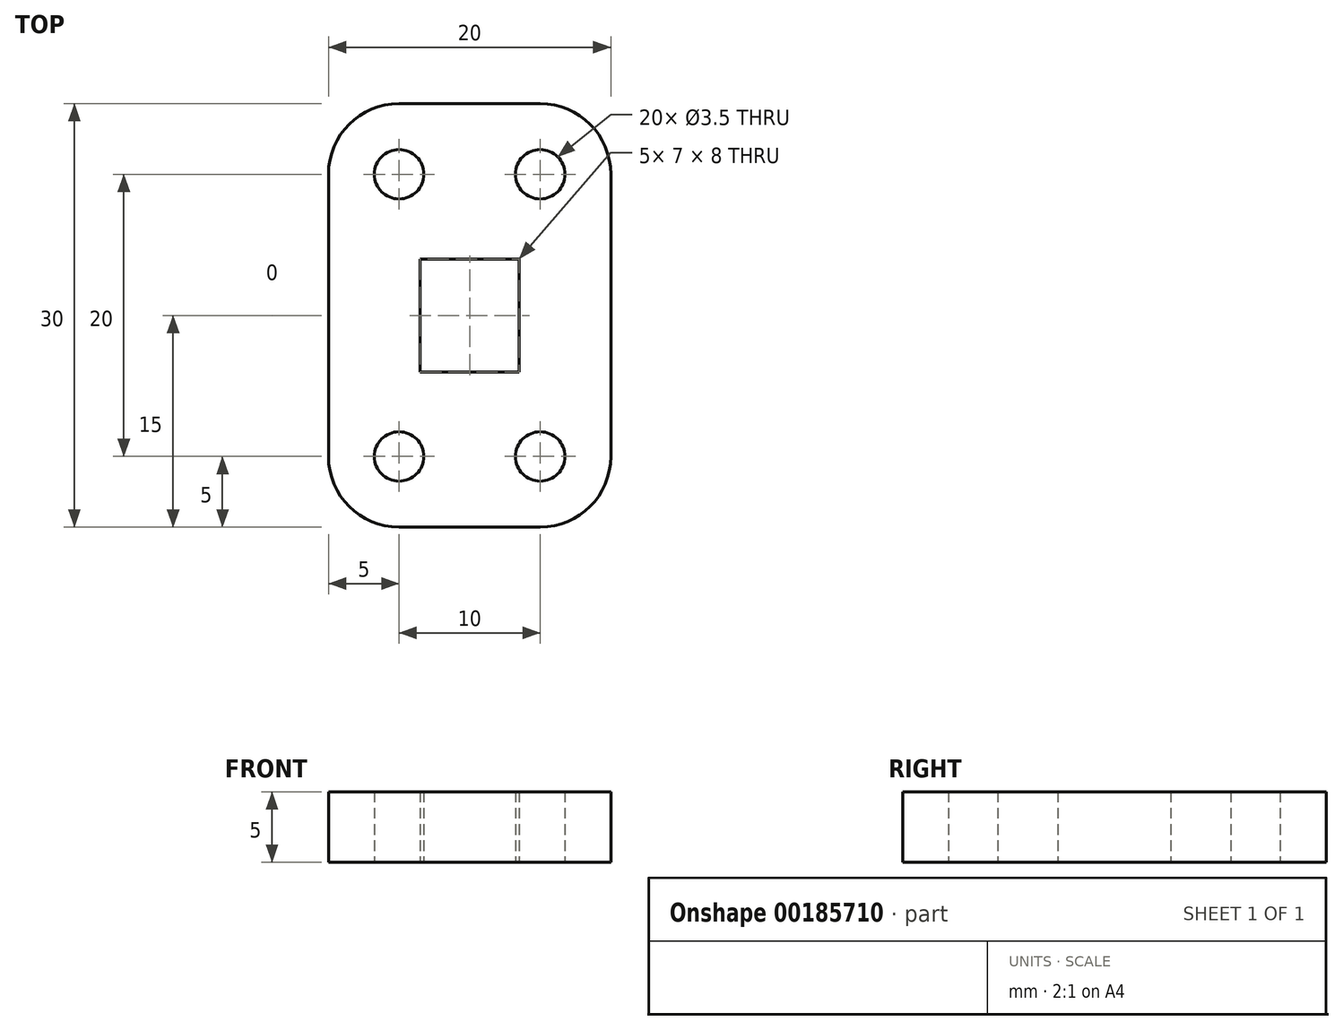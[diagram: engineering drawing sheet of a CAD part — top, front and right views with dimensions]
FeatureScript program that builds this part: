
annotation { "Feature Type Name" : "Feature", "Feature Type Description" : "" }
export const myFeature = defineFeature(function(context is Context, id is Id, definition is map)
    precondition{}
    {
        {
            var Q0;
            Q0=qCreatedBy(makeId("Top.planeOp"),FACE);
            var sketch = newSketch(context, id + "F0", { "sketchPlane" : qUnion([Q0])});
            skPoint(sketch, "E0.middle", {"position": v(0, 0) * mm});
            skLineSegment(sketch, "E1.0", {"start": v(-10, 10) * mm, "end": v(-10, -10) * mm});
            skLineSegment(sketch, "E1.1", {"start": v(5, 15) * mm, "end": v(-5, 15) * mm});
            skLineSegment(sketch, "E1.2", {"start": v(10, 10) * mm, "end": v(10, -10) * mm});
            skLineSegment(sketch, "E1.3", {"start": v(5, -15) * mm, "end": v(-5, -15) * mm});
            skCircle(sketch, "E2", {"center": v(-5, 10) * mm, "radius": 1.75 * mm});
            skCircle(sketch, "E3", {"center": v(5, 10) * mm, "radius": 1.75 * mm});
            skCircle(sketch, "E4", {"center": v(-5, -10) * mm, "radius": 1.75 * mm});
            skCircle(sketch, "E5", {"center": v(5, -10) * mm, "radius": 1.75 * mm});
            skPoint(sketch, "E6.visualSharp", {"position": v(-10, 15) * mm});
            skArc(sketch, "E6.filletArc", {"start": v(-5, 15) * mm, "mid": v(-8.54, 13.54) * mm, "end": v(-10, 10) * mm});
            skPoint(sketch, "E7.visualSharp", {"position": v(10, 15) * mm});
            skArc(sketch, "E7.filletArc", {"start": v(10, 10) * mm, "mid": v(8.54, 13.54) * mm, "end": v(5, 15) * mm});
            skPoint(sketch, "E8.visualSharp", {"position": v(10, -15) * mm});
            skArc(sketch, "E8.filletArc", {"start": v(5, -15) * mm, "mid": v(8.54, -13.54) * mm, "end": v(10, -10) * mm});
            skPoint(sketch, "E9.visualSharp", {"position": v(-10, -15) * mm});
            skArc(sketch, "E9.filletArc", {"start": v(-10, -10) * mm, "mid": v(-8.54, -13.54) * mm, "end": v(-5, -15) * mm});
            skLineSegment(sketch, "E10.bottom", {"start": v(3.5, 4) * mm, "end": v(-3.5, 4) * mm});
            skLineSegment(sketch, "E10.top", {"start": v(3.5, -4) * mm, "end": v(-3.5, -4) * mm});
            skLineSegment(sketch, "E10.left", {"start": v(3.5, 4) * mm, "end": v(3.5, -4) * mm});
            skLineSegment(sketch, "E10.right", {"start": v(-3.5, 4) * mm, "end": v(-3.5, -4) * mm});
            skSolve(sketch);
        }
        {
            var Q0;
            Q0=makeQuery(id+"F0.imprint","IMPRINT",FACE,{"disambiguationData":[TD([[makeQuery(id+"F0.imprint","IMPRINT",EDGE,{"derivedFrom":sQuery(id+"F0.wireOp",EDGE,"E1.0")}),1.0]])]});
            extrude(context, id + "F1", {"entities" : qUnion([Q0]), "depth" : 5 * mm});
        }
    });
